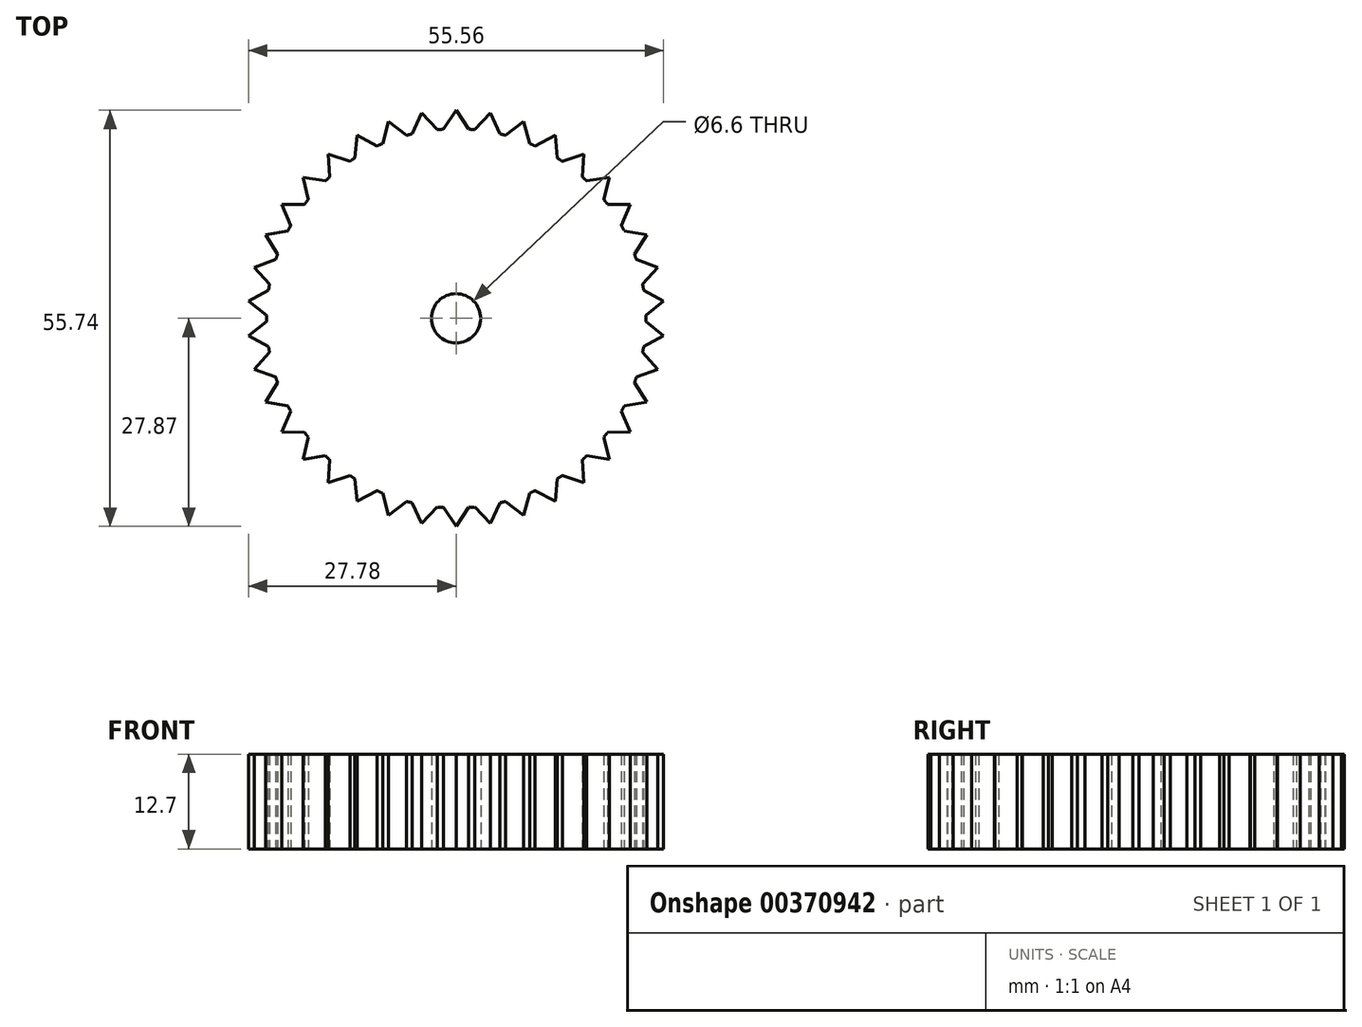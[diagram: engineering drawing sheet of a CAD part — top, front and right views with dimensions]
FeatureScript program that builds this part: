
annotation { "Feature Type Name" : "Feature", "Feature Type Description" : "" }
export const myFeature = defineFeature(function(context is Context, id is Id, definition is map)
    precondition{}
    {
        {
            var Q0;
            Q0=qCreatedBy(makeId("Top.planeOp"),FACE);
            var sketch = newSketch(context, id + "F0", { "sketchPlane" : qUnion([Q0])});
            skCircle(sketch, "E0", {"center": v(0, 0) * mm, "radius": 25.4 * mm});
            skCircle(sketch, "E1", {"center": v(0, 0) * mm, "radius": 3.3 * mm});
            skLineSegment(sketch, "E2", {"start": v(0, 27.87) * mm, "end": v(1.7, 25.34) * mm});
            skLineSegment(sketch, "E3", {"start": v(0, 27.87) * mm, "end": v(-1.7, 25.34) * mm});
            skLineSegment(sketch, "E4.1.0", {"start": v(-4.59, 27.5) * mm, "end": v(-5.85, 24.72) * mm});
            skLineSegment(sketch, "E4.1.1", {"start": v(-4.59, 27.5) * mm, "end": v(-2.5, 25.28) * mm});
            skLineSegment(sketch, "E4.2.0", {"start": v(-9.05, 26.36) * mm, "end": v(-9.84, 23.42) * mm});
            skLineSegment(sketch, "E4.2.1", {"start": v(-9.05, 26.36) * mm, "end": v(-6.62, 24.52) * mm});
            skLineSegment(sketch, "E4.3.0", {"start": v(-13.26, 24.51) * mm, "end": v(-13.56, 21.48) * mm});
            skLineSegment(sketch, "E4.3.1", {"start": v(-13.26, 24.51) * mm, "end": v(-10.56, 23.1) * mm});
            skLineSegment(sketch, "E4.4.0", {"start": v(-17.12, 22) * mm, "end": v(-16.9, 18.95) * mm});
            skLineSegment(sketch, "E4.4.1", {"start": v(-17.12, 22) * mm, "end": v(-14.22, 21.05) * mm});
            skLineSegment(sketch, "E4.5.0", {"start": v(-20.5, 18.88) * mm, "end": v(-19.8, 15.91) * mm});
            skLineSegment(sketch, "E4.5.1", {"start": v(-20.5, 18.88) * mm, "end": v(-17.5, 18.42) * mm});
            skLineSegment(sketch, "E4.6.0", {"start": v(-23.33, 15.24) * mm, "end": v(-22.15, 12.44) * mm});
            skLineSegment(sketch, "E4.6.1", {"start": v(-23.33, 15.24) * mm, "end": v(-20.28, 15.29) * mm});
            skLineSegment(sketch, "E4.7.0", {"start": v(-25.52, 11.2) * mm, "end": v(-23.9, 8.62) * mm});
            skLineSegment(sketch, "E4.7.1", {"start": v(-25.52, 11.2) * mm, "end": v(-22.52, 11.74) * mm});
            skLineSegment(sketch, "E4.8.0", {"start": v(-27.02, 6.84) * mm, "end": v(-24.99, 4.57) * mm});
            skLineSegment(sketch, "E4.8.1", {"start": v(-27.02, 6.84) * mm, "end": v(-24.15, 7.87) * mm});
            skLineSegment(sketch, "E4.9.0", {"start": v(-27.78, 2.3) * mm, "end": v(-25.4, 0.4) * mm});
            skLineSegment(sketch, "E4.9.1", {"start": v(-27.78, 2.3) * mm, "end": v(-25.12, 3.8) * mm});
            skLineSegment(sketch, "E4.10.0", {"start": v(-27.78, -2.3) * mm, "end": v(-25.12, -3.8) * mm});
            skLineSegment(sketch, "E4.10.1", {"start": v(-27.78, -2.3) * mm, "end": v(-25.4, -0.4) * mm});
            skLineSegment(sketch, "E4.11.0", {"start": v(-27.02, -6.84) * mm, "end": v(-24.15, -7.87) * mm});
            skLineSegment(sketch, "E4.11.1", {"start": v(-27.02, -6.84) * mm, "end": v(-24.99, -4.57) * mm});
            skLineSegment(sketch, "E4.12.0", {"start": v(-25.52, -11.2) * mm, "end": v(-22.52, -11.74) * mm});
            skLineSegment(sketch, "E4.12.1", {"start": v(-25.52, -11.2) * mm, "end": v(-23.9, -8.62) * mm});
            skLineSegment(sketch, "E4.13.0", {"start": v(-23.33, -15.24) * mm, "end": v(-20.28, -15.29) * mm});
            skLineSegment(sketch, "E4.13.1", {"start": v(-23.33, -15.24) * mm, "end": v(-22.15, -12.44) * mm});
            skLineSegment(sketch, "E4.14.0", {"start": v(-20.5, -18.88) * mm, "end": v(-17.5, -18.42) * mm});
            skLineSegment(sketch, "E4.14.1", {"start": v(-20.5, -18.88) * mm, "end": v(-19.8, -15.91) * mm});
            skLineSegment(sketch, "E4.15.0", {"start": v(-17.12, -22) * mm, "end": v(-14.22, -21.05) * mm});
            skLineSegment(sketch, "E4.15.1", {"start": v(-17.12, -22) * mm, "end": v(-16.9, -18.95) * mm});
            skLineSegment(sketch, "E4.16.0", {"start": v(-13.26, -24.51) * mm, "end": v(-10.56, -23.1) * mm});
            skLineSegment(sketch, "E4.16.1", {"start": v(-13.26, -24.51) * mm, "end": v(-13.56, -21.48) * mm});
            skLineSegment(sketch, "E4.17.0", {"start": v(-9.05, -26.36) * mm, "end": v(-6.62, -24.52) * mm});
            skLineSegment(sketch, "E4.17.1", {"start": v(-9.05, -26.36) * mm, "end": v(-9.84, -23.42) * mm});
            skLineSegment(sketch, "E4.18.0", {"start": v(-4.59, -27.5) * mm, "end": v(-2.5, -25.28) * mm});
            skLineSegment(sketch, "E4.18.1", {"start": v(-4.59, -27.5) * mm, "end": v(-5.85, -24.72) * mm});
            skLineSegment(sketch, "E4.19.0", {"start": v(0, -27.87) * mm, "end": v(1.7, -25.34) * mm});
            skLineSegment(sketch, "E4.19.1", {"start": v(0, -27.87) * mm, "end": v(-1.7, -25.34) * mm});
            skLineSegment(sketch, "E4.20.0", {"start": v(4.59, -27.5) * mm, "end": v(5.85, -24.72) * mm});
            skLineSegment(sketch, "E4.20.1", {"start": v(4.59, -27.5) * mm, "end": v(2.5, -25.28) * mm});
            skLineSegment(sketch, "E4.21.0", {"start": v(9.05, -26.36) * mm, "end": v(9.84, -23.42) * mm});
            skLineSegment(sketch, "E4.21.1", {"start": v(9.05, -26.36) * mm, "end": v(6.62, -24.52) * mm});
            skLineSegment(sketch, "E4.22.0", {"start": v(13.26, -24.51) * mm, "end": v(13.56, -21.48) * mm});
            skLineSegment(sketch, "E4.22.1", {"start": v(13.26, -24.51) * mm, "end": v(10.56, -23.1) * mm});
            skLineSegment(sketch, "E4.23.0", {"start": v(17.12, -22) * mm, "end": v(16.9, -18.95) * mm});
            skLineSegment(sketch, "E4.23.1", {"start": v(17.12, -22) * mm, "end": v(14.22, -21.05) * mm});
            skLineSegment(sketch, "E4.24.0", {"start": v(20.5, -18.88) * mm, "end": v(19.8, -15.91) * mm});
            skLineSegment(sketch, "E4.24.1", {"start": v(20.5, -18.88) * mm, "end": v(17.5, -18.42) * mm});
            skLineSegment(sketch, "E4.25.0", {"start": v(23.33, -15.24) * mm, "end": v(22.15, -12.44) * mm});
            skLineSegment(sketch, "E4.25.1", {"start": v(23.33, -15.24) * mm, "end": v(20.28, -15.29) * mm});
            skLineSegment(sketch, "E4.26.0", {"start": v(25.52, -11.2) * mm, "end": v(23.9, -8.62) * mm});
            skLineSegment(sketch, "E4.26.1", {"start": v(25.52, -11.2) * mm, "end": v(22.52, -11.74) * mm});
            skLineSegment(sketch, "E4.27.0", {"start": v(27.02, -6.84) * mm, "end": v(24.99, -4.57) * mm});
            skLineSegment(sketch, "E4.27.1", {"start": v(27.02, -6.84) * mm, "end": v(24.15, -7.87) * mm});
            skLineSegment(sketch, "E4.28.0", {"start": v(27.78, -2.3) * mm, "end": v(25.4, -0.4) * mm});
            skLineSegment(sketch, "E4.28.1", {"start": v(27.78, -2.3) * mm, "end": v(25.12, -3.8) * mm});
            skLineSegment(sketch, "E4.29.0", {"start": v(27.78, 2.3) * mm, "end": v(25.12, 3.8) * mm});
            skLineSegment(sketch, "E4.29.1", {"start": v(27.78, 2.3) * mm, "end": v(25.4, 0.4) * mm});
            skLineSegment(sketch, "E4.30.0", {"start": v(27.02, 6.84) * mm, "end": v(24.15, 7.87) * mm});
            skLineSegment(sketch, "E4.30.1", {"start": v(27.02, 6.84) * mm, "end": v(24.99, 4.57) * mm});
            skLineSegment(sketch, "E4.31.0", {"start": v(25.52, 11.2) * mm, "end": v(22.52, 11.74) * mm});
            skLineSegment(sketch, "E4.31.1", {"start": v(25.52, 11.2) * mm, "end": v(23.9, 8.62) * mm});
            skLineSegment(sketch, "E4.32.0", {"start": v(23.33, 15.24) * mm, "end": v(20.28, 15.29) * mm});
            skLineSegment(sketch, "E4.32.1", {"start": v(23.33, 15.24) * mm, "end": v(22.15, 12.44) * mm});
            skLineSegment(sketch, "E4.33.0", {"start": v(20.5, 18.88) * mm, "end": v(17.5, 18.42) * mm});
            skLineSegment(sketch, "E4.33.1", {"start": v(20.5, 18.88) * mm, "end": v(19.8, 15.91) * mm});
            skLineSegment(sketch, "E4.34.0", {"start": v(17.12, 22) * mm, "end": v(14.22, 21.05) * mm});
            skLineSegment(sketch, "E4.34.1", {"start": v(17.12, 22) * mm, "end": v(16.9, 18.95) * mm});
            skLineSegment(sketch, "E4.35.0", {"start": v(13.26, 24.51) * mm, "end": v(10.56, 23.1) * mm});
            skLineSegment(sketch, "E4.35.1", {"start": v(13.26, 24.51) * mm, "end": v(13.56, 21.48) * mm});
            skLineSegment(sketch, "E4.36.0", {"start": v(9.05, 26.36) * mm, "end": v(6.62, 24.52) * mm});
            skLineSegment(sketch, "E4.36.1", {"start": v(9.05, 26.36) * mm, "end": v(9.84, 23.42) * mm});
            skLineSegment(sketch, "E4.37.0", {"start": v(4.59, 27.5) * mm, "end": v(2.5, 25.28) * mm});
            skLineSegment(sketch, "E4.37.1", {"start": v(4.59, 27.5) * mm, "end": v(5.85, 24.72) * mm});
            skSolve(sketch);
        }
        {
            var Q0;
            Q0=makeQuery(id+"F0.imprint","IMPRINT",FACE,{"disambiguationData":[TD([[makeQuery(id+"F0.imprint","IMPRINT",EDGE,{"derivedFrom":sQuery(id+"F0.wireOp",EDGE,"E1")}),-1.0]])]});
            var Q1;
            {var subQ0=sQuery(id+"F0.wireOp",EDGE,"E4.10.0");Q1=makeQuery(id+"F0.imprint","IMPRINT",FACE,{"disambiguationData":[TD([[makeQuery(id+"F0.imprint","IMPRINT",EDGE,{"derivedFrom":subQ0}),1.0]])]});}
            var Q2;
            {var subQ0=sQuery(id+"F0.wireOp",EDGE,"E4.26.0");Q2=makeQuery(id+"F0.imprint","IMPRINT",FACE,{"disambiguationData":[TD([[makeQuery(id+"F0.imprint","IMPRINT",EDGE,{"derivedFrom":subQ0}),1.0]])]});}
            var Q3;
            {var subQ0=sQuery(id+"F0.wireOp",EDGE,"E4.17.0");Q3=makeQuery(id+"F0.imprint","IMPRINT",FACE,{"disambiguationData":[TD([[makeQuery(id+"F0.imprint","IMPRINT",EDGE,{"derivedFrom":subQ0}),1.0]])]});}
            var Q4;
            {var subQ0=sQuery(id+"F0.wireOp",EDGE,"E4.11.0");Q4=makeQuery(id+"F0.imprint","IMPRINT",FACE,{"disambiguationData":[TD([[makeQuery(id+"F0.imprint","IMPRINT",EDGE,{"derivedFrom":subQ0}),1.0]])]});}
            var Q5;
            {var subQ0=sQuery(id+"F0.wireOp",EDGE,"E4.20.0");Q5=makeQuery(id+"F0.imprint","IMPRINT",FACE,{"disambiguationData":[TD([[makeQuery(id+"F0.imprint","IMPRINT",EDGE,{"derivedFrom":subQ0}),1.0]])]});}
            var Q6;
            {var subQ0=sQuery(id+"F0.wireOp",EDGE,"E4.27.0");Q6=makeQuery(id+"F0.imprint","IMPRINT",FACE,{"disambiguationData":[TD([[makeQuery(id+"F0.imprint","IMPRINT",EDGE,{"derivedFrom":subQ0}),1.0]])]});}
            var Q7;
            {var subQ0=sQuery(id+"F0.wireOp",EDGE,"E4.18.0");Q7=makeQuery(id+"F0.imprint","IMPRINT",FACE,{"disambiguationData":[TD([[makeQuery(id+"F0.imprint","IMPRINT",EDGE,{"derivedFrom":subQ0}),1.0]])]});}
            var Q8;
            {var subQ0=sQuery(id+"F0.wireOp",EDGE,"E4.12.0");Q8=makeQuery(id+"F0.imprint","IMPRINT",FACE,{"disambiguationData":[TD([[makeQuery(id+"F0.imprint","IMPRINT",EDGE,{"derivedFrom":subQ0}),1.0]])]});}
            var Q9;
            {var subQ0=sQuery(id+"F0.wireOp",EDGE,"E4.28.0");Q9=makeQuery(id+"F0.imprint","IMPRINT",FACE,{"disambiguationData":[TD([[makeQuery(id+"F0.imprint","IMPRINT",EDGE,{"derivedFrom":subQ0}),1.0]])]});}
            var Q10;
            {var subQ0=sQuery(id+"F0.wireOp",EDGE,"E4.21.0");Q10=makeQuery(id+"F0.imprint","IMPRINT",FACE,{"disambiguationData":[TD([[makeQuery(id+"F0.imprint","IMPRINT",EDGE,{"derivedFrom":subQ0}),1.0]])]});}
            var Q11;
            {var subQ0=sQuery(id+"F0.wireOp",EDGE,"E4.19.0");Q11=makeQuery(id+"F0.imprint","IMPRINT",FACE,{"disambiguationData":[TD([[makeQuery(id+"F0.imprint","IMPRINT",EDGE,{"derivedFrom":subQ0}),1.0]])]});}
            var Q12;
            {var subQ0=sQuery(id+"F0.wireOp",EDGE,"E4.13.0");Q12=makeQuery(id+"F0.imprint","IMPRINT",FACE,{"disambiguationData":[TD([[makeQuery(id+"F0.imprint","IMPRINT",EDGE,{"derivedFrom":subQ0}),1.0]])]});}
            var Q13;
            {var subQ0=sQuery(id+"F0.wireOp",EDGE,"E4.6.0");Q13=makeQuery(id+"F0.imprint","IMPRINT",FACE,{"disambiguationData":[TD([[makeQuery(id+"F0.imprint","IMPRINT",EDGE,{"derivedFrom":subQ0}),1.0]])]});}
            var Q14;
            {var subQ0=sQuery(id+"F0.wireOp",EDGE,"E4.4.0");Q14=makeQuery(id+"F0.imprint","IMPRINT",FACE,{"disambiguationData":[TD([[makeQuery(id+"F0.imprint","IMPRINT",EDGE,{"derivedFrom":subQ0}),1.0]])]});}
            var Q15;
            {var subQ0=sQuery(id+"F0.wireOp",EDGE,"E4.5.0");Q15=makeQuery(id+"F0.imprint","IMPRINT",FACE,{"disambiguationData":[TD([[makeQuery(id+"F0.imprint","IMPRINT",EDGE,{"derivedFrom":subQ0}),1.0]])]});}
            var Q16;
            {var subQ0=sQuery(id+"F0.wireOp",EDGE,"E4.7.0");Q16=makeQuery(id+"F0.imprint","IMPRINT",FACE,{"disambiguationData":[TD([[makeQuery(id+"F0.imprint","IMPRINT",EDGE,{"derivedFrom":subQ0}),1.0]])]});}
            var Q17;
            {var subQ0=sQuery(id+"F0.wireOp",EDGE,"E4.23.0");Q17=makeQuery(id+"F0.imprint","IMPRINT",FACE,{"disambiguationData":[TD([[makeQuery(id+"F0.imprint","IMPRINT",EDGE,{"derivedFrom":subQ0}),1.0]])]});}
            var Q18;
            {var subQ0=sQuery(id+"F0.wireOp",EDGE,"E4.29.0");Q18=makeQuery(id+"F0.imprint","IMPRINT",FACE,{"disambiguationData":[TD([[makeQuery(id+"F0.imprint","IMPRINT",EDGE,{"derivedFrom":subQ0}),1.0]])]});}
            var Q19;
            {var subQ0=sQuery(id+"F0.wireOp",EDGE,"E4.30.0");Q19=makeQuery(id+"F0.imprint","IMPRINT",FACE,{"disambiguationData":[TD([[makeQuery(id+"F0.imprint","IMPRINT",EDGE,{"derivedFrom":subQ0}),1.0]])]});}
            var Q20;
            {var subQ0=sQuery(id+"F0.wireOp",EDGE,"E4.31.0");Q20=makeQuery(id+"F0.imprint","IMPRINT",FACE,{"disambiguationData":[TD([[makeQuery(id+"F0.imprint","IMPRINT",EDGE,{"derivedFrom":subQ0}),1.0]])]});}
            var Q21;
            {var subQ0=sQuery(id+"F0.wireOp",EDGE,"E4.32.0");Q21=makeQuery(id+"F0.imprint","IMPRINT",FACE,{"disambiguationData":[TD([[makeQuery(id+"F0.imprint","IMPRINT",EDGE,{"derivedFrom":subQ0}),1.0]])]});}
            var Q22;
            {var subQ0=sQuery(id+"F0.wireOp",EDGE,"E4.33.0");Q22=makeQuery(id+"F0.imprint","IMPRINT",FACE,{"disambiguationData":[TD([[makeQuery(id+"F0.imprint","IMPRINT",EDGE,{"derivedFrom":subQ0}),1.0]])]});}
            var Q23;
            {var subQ0=sQuery(id+"F0.wireOp",EDGE,"E4.34.0");Q23=makeQuery(id+"F0.imprint","IMPRINT",FACE,{"disambiguationData":[TD([[makeQuery(id+"F0.imprint","IMPRINT",EDGE,{"derivedFrom":subQ0}),1.0]])]});}
            var Q24;
            {var subQ0=sQuery(id+"F0.wireOp",EDGE,"E4.35.0");Q24=makeQuery(id+"F0.imprint","IMPRINT",FACE,{"disambiguationData":[TD([[makeQuery(id+"F0.imprint","IMPRINT",EDGE,{"derivedFrom":subQ0}),1.0]])]});}
            var Q25;
            {var subQ0=sQuery(id+"F0.wireOp",EDGE,"E4.36.0");Q25=makeQuery(id+"F0.imprint","IMPRINT",FACE,{"disambiguationData":[TD([[makeQuery(id+"F0.imprint","IMPRINT",EDGE,{"derivedFrom":subQ0}),1.0]])]});}
            var Q26;
            {var subQ0=sQuery(id+"F0.wireOp",EDGE,"E4.37.0");Q26=makeQuery(id+"F0.imprint","IMPRINT",FACE,{"disambiguationData":[TD([[makeQuery(id+"F0.imprint","IMPRINT",EDGE,{"derivedFrom":subQ0}),1.0]])]});}
            var Q27;
            {var subQ0=sQuery(id+"F0.wireOp",EDGE,"E2");Q27=makeQuery(id+"F0.imprint","IMPRINT",FACE,{"disambiguationData":[TD([[makeQuery(id+"F0.imprint","IMPRINT",EDGE,{"derivedFrom":subQ0}),-1.0]])]});}
            var Q28;
            {var subQ0=sQuery(id+"F0.wireOp",EDGE,"E4.1.0");Q28=makeQuery(id+"F0.imprint","IMPRINT",FACE,{"disambiguationData":[TD([[makeQuery(id+"F0.imprint","IMPRINT",EDGE,{"derivedFrom":subQ0}),1.0]])]});}
            var Q29;
            {var subQ0=sQuery(id+"F0.wireOp",EDGE,"E4.2.0");Q29=makeQuery(id+"F0.imprint","IMPRINT",FACE,{"disambiguationData":[TD([[makeQuery(id+"F0.imprint","IMPRINT",EDGE,{"derivedFrom":subQ0}),1.0]])]});}
            var Q30;
            {var subQ0=sQuery(id+"F0.wireOp",EDGE,"E4.3.0");Q30=makeQuery(id+"F0.imprint","IMPRINT",FACE,{"disambiguationData":[TD([[makeQuery(id+"F0.imprint","IMPRINT",EDGE,{"derivedFrom":subQ0}),1.0]])]});}
            var Q31;
            {var subQ0=sQuery(id+"F0.wireOp",EDGE,"E4.14.0");Q31=makeQuery(id+"F0.imprint","IMPRINT",FACE,{"disambiguationData":[TD([[makeQuery(id+"F0.imprint","IMPRINT",EDGE,{"derivedFrom":subQ0}),1.0]])]});}
            var Q32;
            {var subQ0=sQuery(id+"F0.wireOp",EDGE,"E4.8.0");Q32=makeQuery(id+"F0.imprint","IMPRINT",FACE,{"disambiguationData":[TD([[makeQuery(id+"F0.imprint","IMPRINT",EDGE,{"derivedFrom":subQ0}),1.0]])]});}
            var Q33;
            {var subQ0=sQuery(id+"F0.wireOp",EDGE,"E4.24.0");Q33=makeQuery(id+"F0.imprint","IMPRINT",FACE,{"disambiguationData":[TD([[makeQuery(id+"F0.imprint","IMPRINT",EDGE,{"derivedFrom":subQ0}),1.0]])]});}
            var Q34;
            {var subQ0=sQuery(id+"F0.wireOp",EDGE,"E4.15.0");Q34=makeQuery(id+"F0.imprint","IMPRINT",FACE,{"disambiguationData":[TD([[makeQuery(id+"F0.imprint","IMPRINT",EDGE,{"derivedFrom":subQ0}),1.0]])]});}
            var Q35;
            {var subQ0=sQuery(id+"F0.wireOp",EDGE,"E4.9.0");Q35=makeQuery(id+"F0.imprint","IMPRINT",FACE,{"disambiguationData":[TD([[makeQuery(id+"F0.imprint","IMPRINT",EDGE,{"derivedFrom":subQ0}),1.0]])]});}
            var Q36;
            {var subQ0=sQuery(id+"F0.wireOp",EDGE,"E4.25.0");Q36=makeQuery(id+"F0.imprint","IMPRINT",FACE,{"disambiguationData":[TD([[makeQuery(id+"F0.imprint","IMPRINT",EDGE,{"derivedFrom":subQ0}),1.0]])]});}
            var Q37;
            {var subQ0=sQuery(id+"F0.wireOp",EDGE,"E4.22.0");Q37=makeQuery(id+"F0.imprint","IMPRINT",FACE,{"disambiguationData":[TD([[makeQuery(id+"F0.imprint","IMPRINT",EDGE,{"derivedFrom":subQ0}),1.0]])]});}
            var Q38;
            {var subQ0=sQuery(id+"F0.wireOp",EDGE,"E4.16.0");Q38=makeQuery(id+"F0.imprint","IMPRINT",FACE,{"disambiguationData":[TD([[makeQuery(id+"F0.imprint","IMPRINT",EDGE,{"derivedFrom":subQ0}),1.0]])]});}
            extrude(context, id + "F1", {"entities" : qUnion([Q0, Q1, Q2, Q3, Q4, Q5, Q6, Q7, Q8, Q9, Q10, Q11, Q12, Q13, Q14, Q15, Q16, Q17, Q18, Q19, Q20, Q21, Q22, Q23, Q24, Q25, Q26, Q27, Q28, Q29, Q30, Q31, Q32, Q33, Q34, Q35, Q36, Q37, Q38]), "depth" : 12.7 * mm});
        }
    });
